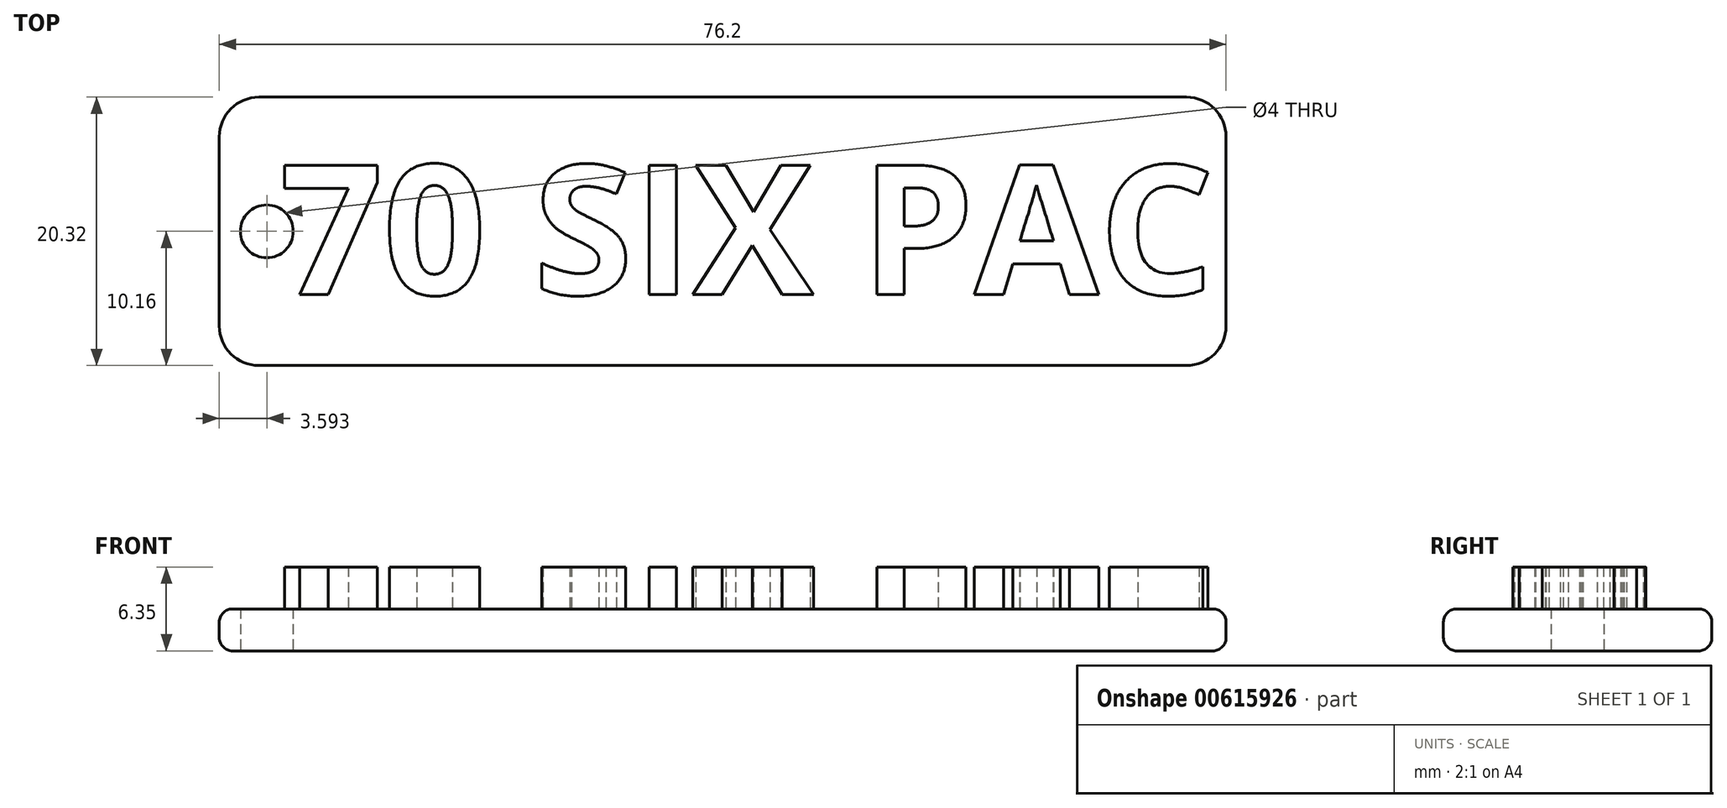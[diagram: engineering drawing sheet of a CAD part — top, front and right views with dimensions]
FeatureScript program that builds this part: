
annotation { "Feature Type Name" : "Feature", "Feature Type Description" : "" }
export const myFeature = defineFeature(function(context is Context, id is Id, definition is map)
    precondition{}
    {
        {
            var Q0;
            Q0=qCreatedBy(makeId("Top.planeOp"),FACE);
            var sketch = newSketch(context, id + "F0", { "sketchPlane" : qUnion([Q0])});
            skLineSegment(sketch, "E0.bottom", {"start": v(35.1, 10.16) * mm, "end": v(-35.1, 10.16) * mm});
            skLineSegment(sketch, "E0.top", {"start": v(35.1, -10.16) * mm, "end": v(-35.1, -10.16) * mm});
            skLineSegment(sketch, "E0.left", {"start": v(38.1, 7.16) * mm, "end": v(38.1, -7.16) * mm});
            skLineSegment(sketch, "E0.right", {"start": v(-38.1, 7.16) * mm, "end": v(-38.1, -7.16) * mm});
            skPoint(sketch, "E0.middle", {"position": v(0, 0) * mm});
            skCircle(sketch, "E1", {"center": v(-34.5, 0) * mm, "radius": 2 * mm});
            skPoint(sketch, "E1.centerSnap0", {"position": v(-38.1, 0) * mm});
            skPoint(sketch, "E2.orphan", {"position": v(38.1, 10.16) * mm});
            skPoint(sketch, "E3.orphan", {"position": v(38.1, -10.16) * mm});
            skPoint(sketch, "E4.visualSharp", {"position": v(37.57, -10.16) * mm});
            skArc(sketch, "E4.filletArc", {"start": v(37.58, -10.16) * mm, "mid": v(37.56, -10.16) * mm, "end": v(37.55, -10.16) * mm});
            skArc(sketch, "E5.filletArc", {"start": v(38.1, 7.16) * mm, "mid": v(37.22, 9.28) * mm, "end": v(35.1, 10.16) * mm});
            skArc(sketch, "E6.filletArc", {"start": v(35.1, -10.16) * mm, "mid": v(37.22, -9.28) * mm, "end": v(38.1, -7.16) * mm});
            skPoint(sketch, "E7.visualSharp", {"position": v(-38.1, 10.16) * mm});
            skArc(sketch, "E7.filletArc", {"start": v(-35.1, 10.16) * mm, "mid": v(-37.22, 9.28) * mm, "end": v(-38.1, 7.16) * mm});
            skPoint(sketch, "E8.visualSharp", {"position": v(-38.1, -10.16) * mm});
            skArc(sketch, "E8.filletArc", {"start": v(-38.1, -7.16) * mm, "mid": v(-37.22, -9.28) * mm, "end": v(-35.1, -10.16) * mm});
            skSolve(sketch);
        }
        {
            var Q0;
            Q0=qCreatedBy(makeId("Top.planeOp"),FACE);
            var sketch = newSketch(context, id + "F1", { "sketchPlane" : qUnion([Q0])});
            skText(sketch, "E9", { "text": "70 SIX PAC", "fontName": "OpenSans-Bold.ttf"});
            const initialGuessF1  = {"E9": [-0.03353, -0.00478, 1, 0, 0.00986]};
            skSetInitialGuess(sketch, initialGuessF1);
            skSolve(sketch);
        }
        {
            var Q0;
            Q0 = qSketchRegion(id + "F0", true);
            extrude(context, id + "F2", {"entities" : qUnion([Q0]), "depth" : 3.17 * mm, "offsetDistance" : 25.4 * mm});
        }
        {
            var Q0;
            Q0 = qSketchRegion(id + "F1", true);
            extrude(context, id + "F3", {"entities" : qUnion([Q0]), "operationType" : NewBodyOperationType.ADD, "depth" : 6.35 * mm, "offsetDistance" : 25.4 * mm});
        }
        {
            var Q0;
            Q0=makeQuery(id+"F2.opExtrude","CAP_EDGE",EDGE,{"disambiguationData":[OSD([sQuery(id+"F0.wireOp",EDGE,"E0.bottom")])],"isStart":false});
            fillet(context, id + "F4", {"entities" : qUnion([Q0]), "radius" : 1 * mm, "tangentPropagation" : true, "allowEdgeOverflow" : false});
        }
        {
            var Q0;
            Q0=makeQuery(id+"F2.opExtrude","CAP_EDGE",EDGE,{"disambiguationData":[OSD([sQuery(id+"F0.wireOp",EDGE,"E0.bottom")])],"isStart":true});
            fillet(context, id + "F5", {"entities" : qUnion([Q0]), "radius" : 1 * mm, "tangentPropagation" : true, "allowEdgeOverflow" : false});
        }
    });
